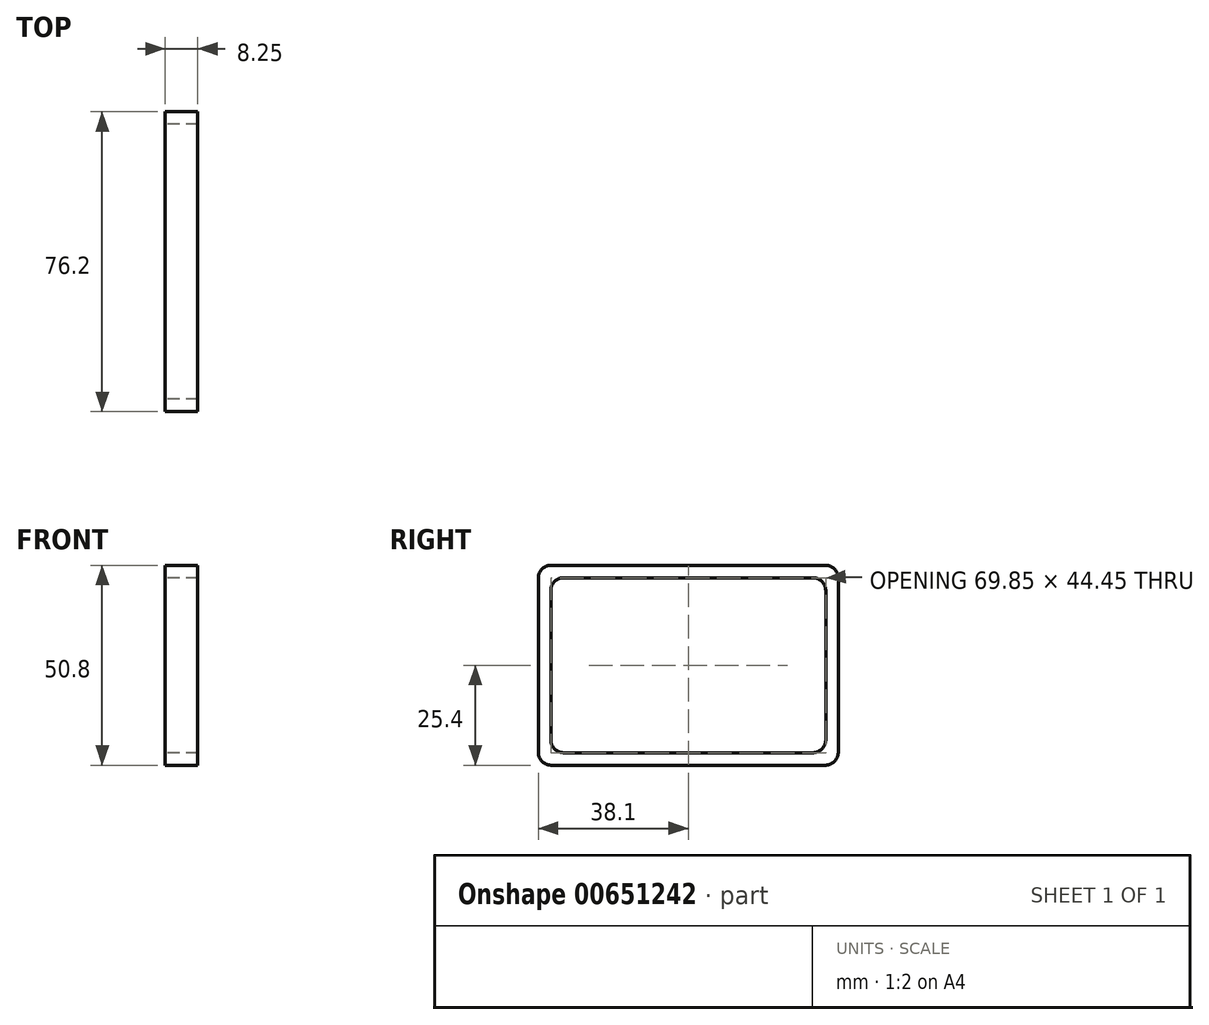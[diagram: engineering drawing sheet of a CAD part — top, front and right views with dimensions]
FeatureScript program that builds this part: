
annotation { "Feature Type Name" : "Feature", "Feature Type Description" : "" }
export const myFeature = defineFeature(function(context is Context, id is Id, definition is map)
    precondition{}
    {
        {
            var Q0;
            Q0=qCreatedBy(makeId("Right.planeOp"),FACE);
            var sketch = newSketch(context, id + "F0", { "sketchPlane" : qUnion([Q0])});
            skLineSegment(sketch, "E0.bottom", {"start": v(38.1, -25.4) * mm, "end": v(-38.1, -25.4) * mm});
            skLineSegment(sketch, "E0.top", {"start": v(38.1, 25.4) * mm, "end": v(-38.1, 25.4) * mm});
            skLineSegment(sketch, "E0.left", {"start": v(38.1, -25.4) * mm, "end": v(38.1, 25.4) * mm});
            skLineSegment(sketch, "E0.right", {"start": v(-38.1, -25.4) * mm, "end": v(-38.1, 25.4) * mm});
            skPoint(sketch, "E0.middle", {"position": v(0, 0) * mm});
            skLineSegment(sketch, "E1.bottom", {"start": v(34.93, -22.22) * mm, "end": v(-34.93, -22.23) * mm});
            skLineSegment(sketch, "E1.top", {"start": v(34.93, 22.23) * mm, "end": v(-34.93, 22.22) * mm});
            skLineSegment(sketch, "E1.left", {"start": v(34.93, -22.22) * mm, "end": v(34.93, 22.23) * mm});
            skLineSegment(sketch, "E1.right", {"start": v(-34.93, -22.23) * mm, "end": v(-34.93, 22.22) * mm});
            skSolve(sketch);
        }
        {
            assignVariable(context, id + "F1", {"name" : "Length", "anyValue" : 8.25});
        }
        {
            var Q0;
            Q0=makeQuery(id+"F0.imprint","IMPRINT",FACE,{"disambiguationData":[TD([[makeQuery(id+"F0.imprint","IMPRINT",EDGE,{"derivedFrom":sQuery(id+"F0.wireOp",EDGE,"E0.bottom")}),-1.0]])]});
            extrude(context, id + "F2", {"entities" : qUnion([Q0]), "depth" : (getVariable(context, 'Length')) * mm, "offsetDistance" : 25.4 * mm});
        }
        {
            var Q0;
            Q0=makeQuery(id+"F2.opExtrude","SWEPT_EDGE",EDGE,{"disambiguationData":[OSD([sQuery(id+"F0.wireOp",EDGE,"E0.top"),sQuery(id+"F0.wireOp",EDGE,"E0.left")])]});
            var Q1;
            Q1=makeQuery(id+"F2.opExtrude","SWEPT_EDGE",EDGE,{"disambiguationData":[OSD([sQuery(id+"F0.wireOp",EDGE,"E0.bottom"),sQuery(id+"F0.wireOp",EDGE,"E0.left")])]});
            var Q2;
            Q2=makeQuery(id+"F2.opExtrude","SWEPT_EDGE",EDGE,{"disambiguationData":[OSD([sQuery(id+"F0.wireOp",EDGE,"E0.bottom"),sQuery(id+"F0.wireOp",EDGE,"E0.right")])]});
            var Q3;
            Q3=makeQuery(id+"F2.opExtrude","SWEPT_EDGE",EDGE,{"disambiguationData":[OSD([sQuery(id+"F0.wireOp",EDGE,"E0.top"),sQuery(id+"F0.wireOp",EDGE,"E0.right")])]});
            var Q4;
            Q4=makeQuery(id+"F2.opExtrude","SWEPT_EDGE",EDGE,{"disambiguationData":[OSD([sQuery(id+"F0.wireOp",EDGE,"E1.bottom"),sQuery(id+"F0.wireOp",EDGE,"E1.left")])]});
            var Q5;
            Q5=makeQuery(id+"F2.opExtrude","SWEPT_EDGE",EDGE,{"disambiguationData":[OSD([sQuery(id+"F0.wireOp",EDGE,"E1.top"),sQuery(id+"F0.wireOp",EDGE,"E1.left")])]});
            var Q6;
            Q6=makeQuery(id+"F2.opExtrude","SWEPT_EDGE",EDGE,{"disambiguationData":[OSD([sQuery(id+"F0.wireOp",EDGE,"E1.top"),sQuery(id+"F0.wireOp",EDGE,"E1.right")])]});
            var Q7;
            Q7=makeQuery(id+"F2.opExtrude","SWEPT_EDGE",EDGE,{"disambiguationData":[OSD([sQuery(id+"F0.wireOp",EDGE,"E1.bottom"),sQuery(id+"F0.wireOp",EDGE,"E1.right")])]});
            fillet(context, id + "F3", {"entities" : qUnion([Q0, Q1, Q2, Q3, Q4, Q5, Q6, Q7]), "radius" : 3.17 * mm, "tangentPropagation" : true, "allowEdgeOverflow" : false});
        }
    });
